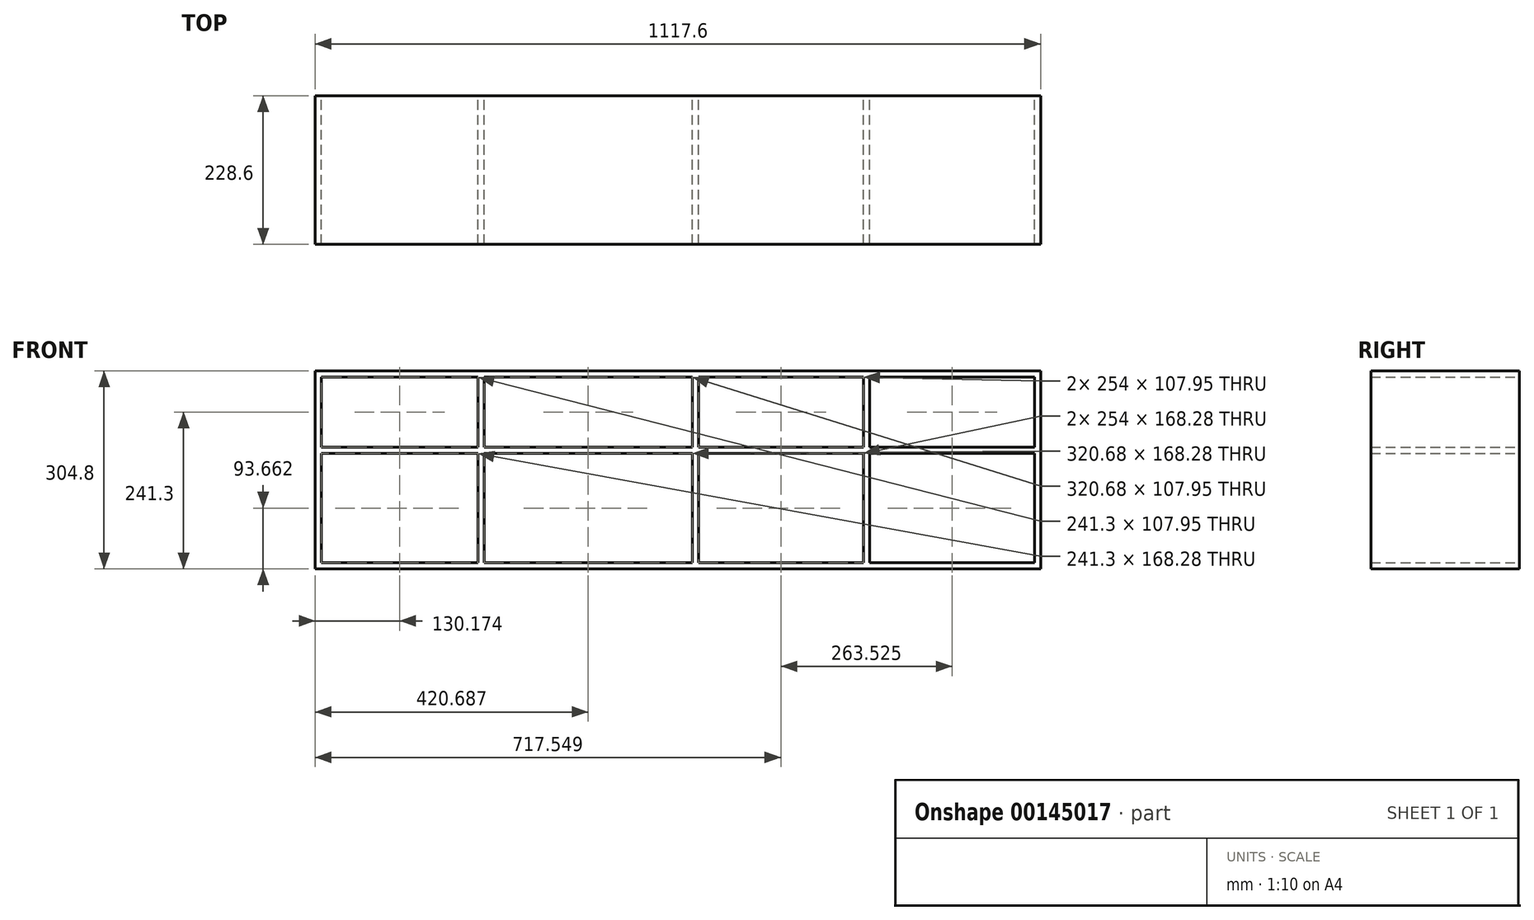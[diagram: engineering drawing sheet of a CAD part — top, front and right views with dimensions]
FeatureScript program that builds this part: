
annotation { "Feature Type Name" : "Feature", "Feature Type Description" : "" }
export const myFeature = defineFeature(function(context is Context, id is Id, definition is map)
    precondition{}
    {
        {
            var Q0;
            Q0=qCreatedBy(makeId("Front.planeOp"),FACE);
            var sketch = newSketch(context, id + "F0", { "sketchPlane" : qUnion([Q0])});
            skLineSegment(sketch, "E0.bottom", {"start": v(-515.76, 0) * mm, "end": v(601.84, 0) * mm});
            skLineSegment(sketch, "E0.top", {"start": v(-515.76, 304.8) * mm, "end": v(601.84, 304.8) * mm});
            skLineSegment(sketch, "E0.left", {"start": v(-515.76, 0) * mm, "end": v(-515.76, 304.8) * mm});
            skLineSegment(sketch, "E0.right", {"start": v(601.84, 0) * mm, "end": v(601.84, 304.8) * mm});
            skLineSegment(sketch, "E1.0", {"start": v(-506.24, 9.53) * mm, "end": v(-506.24, 295.28) * mm});
            skLineSegment(sketch, "E1.1", {"start": v(-506.24, 9.53) * mm, "end": v(592.31, 9.53) * mm});
            skLineSegment(sketch, "E1.2", {"start": v(592.31, 9.53) * mm, "end": v(592.31, 295.28) * mm});
            skLineSegment(sketch, "E1.3", {"start": v(-506.24, 295.28) * mm, "end": v(592.31, 295.28) * mm});
            skLineSegment(sketch, "E2.bottom", {"start": v(-264.94, 177.8) * mm, "end": v(-506.24, 177.8) * mm});
            skLineSegment(sketch, "E2.top", {"start": v(-264.94, 9.53) * mm, "end": v(-506.24, 9.53) * mm});
            skLineSegment(sketch, "E2.left", {"start": v(-264.94, 177.8) * mm, "end": v(-264.94, 9.53) * mm});
            skLineSegment(sketch, "E2.right", {"start": v(-506.24, 177.8) * mm, "end": v(-506.24, 9.53) * mm});
            skLineSegment(sketch, "E3.0", {"start": v(-255.41, 187.32) * mm, "end": v(-506.24, 187.32) * mm});
            skLineSegment(sketch, "E3.1", {"start": v(-255.41, 187.33) * mm, "end": v(-255.41, 9.53) * mm});
            skLineSegment(sketch, "E4", {"start": v(-255.41, 187.33) * mm, "end": v(-255.41, 295.28) * mm});
            skLineSegment(sketch, "E5.0", {"start": v(-264.94, 187.32) * mm, "end": v(-264.94, 295.28) * mm});
            skLineSegment(sketch, "E6", {"start": v(-255.41, 187.32) * mm, "end": v(592.31, 187.32) * mm});
            skLineSegment(sketch, "E7.0", {"start": v(-255.41, 177.8) * mm, "end": v(592.31, 177.8) * mm});
            skLineSegment(sketch, "E8", {"start": v(338.31, 177.8) * mm, "end": v(338.31, 9.53) * mm});
            skLineSegment(sketch, "E9.0", {"start": v(328.79, 177.8) * mm, "end": v(328.79, 9.53) * mm});
            skLineSegment(sketch, "E10", {"start": v(74.79, 177.8) * mm, "end": v(74.79, 9.53) * mm});
            skPoint(sketch, "E10.endSnap0", {"position": v(43.04, 9.53) * mm});
            skLineSegment(sketch, "E11.0", {"start": v(65.26, 177.8) * mm, "end": v(65.26, 9.53) * mm});
            skLineSegment(sketch, "E12", {"start": v(338.31, 177.8) * mm, "end": v(338.31, 295.28) * mm});
            skLineSegment(sketch, "E13", {"start": v(74.79, 177.8) * mm, "end": v(74.79, 295.28) * mm});
            skLineSegment(sketch, "E14.0", {"start": v(328.79, 177.8) * mm, "end": v(328.79, 295.28) * mm});
            skLineSegment(sketch, "E15.0", {"start": v(65.26, 177.8) * mm, "end": v(65.26, 295.28) * mm});
            skSolve(sketch);
        }
        {
            var Q0;
            Q0=makeQuery(id+"F0.imprint","IMPRINT",FACE,{"disambiguationData":[TD([[makeQuery(id+"F0.imprint","IMPRINT",EDGE,{"derivedFrom":sQuery(id+"F0.wireOp",EDGE,"E0.bottom")}),1.0]])]});
            var Q1;
            {var subQ1=sQuery(id+"F0.wireOp",EDGE,"E2.bottom");Q1=makeQuery(id+"F0.imprint","IMPRINT",FACE,{"disambiguationData":[TD([[makeQuery(id+"F0.imprint","IMPRINT",EDGE,{"derivedFrom":subQ1}),-1.0]])]});}
            var Q2;
            {var subQ0=sQuery(id+"F0.wireOp",EDGE,"E4");Q2=makeQuery(id+"F0.imprint","IMPRINT",FACE,{"disambiguationData":[TD([[makeQuery(id+"F0.imprint","IMPRINT",EDGE,{"derivedFrom":subQ0}),1.0]])]});}
            extrude(context, id + "F1", {"entities" : qUnion([Q0, Q1, Q2]), "depth" : 228.6 * mm});
        }
        {
            var Q0;
            {var subQ0=sQuery(id+"F0.wireOp",EDGE,"E6");Q0=makeQuery(id+"F0.imprint","IMPRINT",FACE,{"disambiguationData":[TD([[makeQuery(id+"F0.imprint","IMPRINT",EDGE,{"derivedFrom":subQ0}),-1.0]])]});}
            var Q1;
            Q1=makeQuery(id+"F1.opExtrude","CAP_FACE",FACE,{"disambiguationData":[OSD([sQuery(id+"F0.wireOp",EDGE,"E0.bottom"),sQuery(id+"F0.wireOp",EDGE,"E0.top"),sQuery(id+"F0.wireOp",EDGE,"E0.left"),sQuery(id+"F0.wireOp",EDGE,"E0.right"),sQuery(id+"F0.wireOp",EDGE,"E1.0"),sQuery(id+"F0.wireOp",EDGE,"E1.1"),sQuery(id+"F0.wireOp",EDGE,"E1.2"),sQuery(id+"F0.wireOp",EDGE,"E1.3"),sQuery(id+"F0.wireOp",EDGE,"E2.bottom"),sQuery(id+"F0.wireOp",EDGE,"E2.top"),sQuery(id+"F0.wireOp",EDGE,"E2.left"),sQuery(id+"F0.wireOp",EDGE,"E2.right"),sQuery(id+"F0.wireOp",EDGE,"E3.0"),sQuery(id+"F0.wireOp",EDGE,"E3.1"),sQuery(id+"F0.wireOp",EDGE,"E4"),sQuery(id+"F0.wireOp",EDGE,"E5.0")])],"isStart":false});
            extrude(context, id + "F2", {"entities" : qUnion([Q0]), "operationType" : NewBodyOperationType.ADD, "endBound" : BoundingType.UP_TO_SURFACE, "endBoundEntityFace" : qUnion([Q1]), "depth" : 25.4 * mm});
        }
        {
            var Q0;
            {var subQ0=sQuery(id+"F0.wireOp",EDGE,"E8");Q0=makeQuery(id+"F0.imprint","IMPRINT",FACE,{"disambiguationData":[TD([[makeQuery(id+"F0.imprint","IMPRINT",EDGE,{"derivedFrom":subQ0}),-1.0]])]});}
            var Q1;
            {var subQ0=sQuery(id+"F0.wireOp",EDGE,"E5.0");var subQ1=sQuery(id+"F0.wireOp",EDGE,"E4");var subQ2=sQuery(id+"F0.wireOp",EDGE,"E3.1");var subQ3=sQuery(id+"F0.wireOp",EDGE,"E3.0");var subQ4=sQuery(id+"F0.wireOp",EDGE,"E2.right");var subQ5=sQuery(id+"F0.wireOp",EDGE,"E2.left");var subQ6=sQuery(id+"F0.wireOp",EDGE,"E2.top");var subQ7=sQuery(id+"F0.wireOp",EDGE,"E2.bottom");var subQ8=sQuery(id+"F0.wireOp",EDGE,"E1.3");var subQ9=sQuery(id+"F0.wireOp",EDGE,"E1.2");var subQ10=sQuery(id+"F0.wireOp",EDGE,"E1.1");var subQ11=sQuery(id+"F0.wireOp",EDGE,"E1.0");var subQ12=sQuery(id+"F0.wireOp",EDGE,"E0.right");var subQ13=sQuery(id+"F0.wireOp",EDGE,"E0.left");var subQ14=sQuery(id+"F0.wireOp",EDGE,"E0.top");var subQ15=sQuery(id+"F0.wireOp",EDGE,"E0.bottom");Q1=makeQuery(id+"F2.boolean.opBoolean","MERGE",FACE,{"derivedFrom":[makeQuery(id+"F1.opExtrude","CAP_FACE",FACE,{"disambiguationData":[OSD([subQ15,subQ14,subQ13,subQ12,subQ11,subQ10,subQ9,subQ8,subQ7,subQ6,subQ5,subQ4,subQ3,subQ2,subQ1,subQ0])],"isStart":false}),makeQuery(id+"F2.opExtrude","CAP_FACE",FACE,{"disambiguationData":[OSD([subQ15,subQ14,subQ13,subQ12,subQ11,subQ10,subQ9,subQ8,subQ7,subQ6,subQ5,subQ4,subQ3,subQ2,subQ1,subQ0])],"isStart":false})]});}
            extrude(context, id + "F3", {"entities" : qUnion([Q0]), "operationType" : NewBodyOperationType.ADD, "endBound" : BoundingType.UP_TO_SURFACE, "endBoundEntityFace" : qUnion([Q1]), "depth" : 25.4 * mm});
        }
        {
            var Q0;
            {var subQ1=sQuery(id+"F0.wireOp",EDGE,"E7.0");var subQ4=sQuery(id+"F0.wireOp",EDGE,"E3.1");var subQ5=makeQuery(id+"F0.imprint","INTERSECT",VERTEX,{"derivedFrom":[subQ4,subQ1]});Q0=makeQuery(id+"F0.imprint","IMPRINT",FACE,{"disambiguationData":[TD([[makeQuery(id+"F0.imprint","IMPRINT",EDGE,{"disambiguationData":[TD([[subQ5,-1.0]])],"derivedFrom":subQ1}),1.0]])]});}
            var Q1;
            {var subQ0=sQuery(id+"F0.wireOp",EDGE,"E10");Q1=makeQuery(id+"F0.imprint","IMPRINT",FACE,{"disambiguationData":[TD([[makeQuery(id+"F0.imprint","IMPRINT",EDGE,{"derivedFrom":subQ0}),-1.0]])]});}
            var Q2;
            {var subQ0=sQuery(id+"F0.wireOp",EDGE,"E5.0");var subQ1=sQuery(id+"F0.wireOp",EDGE,"E4");var subQ2=sQuery(id+"F0.wireOp",EDGE,"E3.1");var subQ3=sQuery(id+"F0.wireOp",EDGE,"E3.0");var subQ4=sQuery(id+"F0.wireOp",EDGE,"E2.right");var subQ5=sQuery(id+"F0.wireOp",EDGE,"E2.left");var subQ6=sQuery(id+"F0.wireOp",EDGE,"E2.top");var subQ7=sQuery(id+"F0.wireOp",EDGE,"E2.bottom");var subQ8=sQuery(id+"F0.wireOp",EDGE,"E1.3");var subQ9=sQuery(id+"F0.wireOp",EDGE,"E1.2");var subQ10=sQuery(id+"F0.wireOp",EDGE,"E1.1");var subQ11=sQuery(id+"F0.wireOp",EDGE,"E1.0");var subQ12=sQuery(id+"F0.wireOp",EDGE,"E0.right");var subQ13=sQuery(id+"F0.wireOp",EDGE,"E0.left");var subQ14=sQuery(id+"F0.wireOp",EDGE,"E0.top");var subQ15=sQuery(id+"F0.wireOp",EDGE,"E0.bottom");Q2=makeQuery(id+"F3.boolean.opBoolean","MERGE",FACE,{"derivedFrom":[makeQuery(id+"F2.boolean.opBoolean","MERGE",FACE,{"derivedFrom":[makeQuery(id+"F1.opExtrude","CAP_FACE",FACE,{"disambiguationData":[OSD([subQ15,subQ14,subQ13,subQ12,subQ11,subQ10,subQ9,subQ8,subQ7,subQ6,subQ5,subQ4,subQ3,subQ2,subQ1,subQ0])],"isStart":false}),makeQuery(id+"F2.opExtrude","CAP_FACE",FACE,{"disambiguationData":[OSD([subQ15,subQ14,subQ13,subQ12,subQ11,subQ10,subQ9,subQ8,subQ7,subQ6,subQ5,subQ4,subQ3,subQ2,subQ1,subQ0])],"isStart":false})]}),makeQuery(id+"F3.opExtrude","CAP_FACE",FACE,{"disambiguationData":[OSD([subQ15,subQ14,subQ13,subQ12,subQ11,subQ10,subQ9,subQ8,subQ7,subQ6,subQ5,subQ4,subQ3,subQ2,subQ1,subQ0])],"isStart":false})]});}
            extrude(context, id + "F4", {"entities" : qUnion([Q0, Q1]), "operationType" : NewBodyOperationType.ADD, "endBound" : BoundingType.UP_TO_SURFACE, "endBoundEntityFace" : qUnion([Q2]), "depth" : 25.4 * mm});
        }
        {
            var Q0;
            {var subQ0=sQuery(id+"F0.wireOp",EDGE,"E13");var subQ1=sQuery(id+"F0.wireOp",EDGE,"E1.3");var subQ2=makeQuery(id+"F0.imprint","INTERSECT",VERTEX,{"derivedFrom":[subQ1,subQ0]});Q0=makeQuery(id+"F0.imprint","IMPRINT",FACE,{"disambiguationData":[TD([[makeQuery(id+"F0.imprint","IMPRINT",EDGE,{"disambiguationData":[TD([[subQ2,1.0]])],"derivedFrom":subQ1}),-1.0]])]});}
            var Q1;
            {var subQ0=sQuery(id+"F0.wireOp",EDGE,"E12");var subQ1=sQuery(id+"F0.wireOp",EDGE,"E1.3");var subQ2=makeQuery(id+"F0.imprint","INTERSECT",VERTEX,{"derivedFrom":[subQ1,subQ0]});Q1=makeQuery(id+"F0.imprint","IMPRINT",FACE,{"disambiguationData":[TD([[makeQuery(id+"F0.imprint","IMPRINT",EDGE,{"disambiguationData":[TD([[subQ2,1.0]])],"derivedFrom":subQ1}),-1.0]])]});}
            var Q2;
            {var subQ0=sQuery(id+"F0.wireOp",EDGE,"E1.1");var subQ1=sQuery(id+"F0.wireOp",EDGE,"E5.0");var subQ2=sQuery(id+"F0.wireOp",EDGE,"E4");var subQ3=sQuery(id+"F0.wireOp",EDGE,"E3.1");var subQ4=sQuery(id+"F0.wireOp",EDGE,"E3.0");var subQ5=sQuery(id+"F0.wireOp",EDGE,"E2.right");var subQ6=sQuery(id+"F0.wireOp",EDGE,"E2.left");var subQ7=sQuery(id+"F0.wireOp",EDGE,"E2.top");var subQ8=sQuery(id+"F0.wireOp",EDGE,"E2.bottom");var subQ9=sQuery(id+"F0.wireOp",EDGE,"E1.3");var subQ10=sQuery(id+"F0.wireOp",EDGE,"E1.2");var subQ11=sQuery(id+"F0.wireOp",EDGE,"E1.0");var subQ12=sQuery(id+"F0.wireOp",EDGE,"E0.right");var subQ13=sQuery(id+"F0.wireOp",EDGE,"E0.left");var subQ14=sQuery(id+"F0.wireOp",EDGE,"E0.top");var subQ15=sQuery(id+"F0.wireOp",EDGE,"E0.bottom");Q2=makeQuery(id+"F4.boolean.opBoolean","MERGE",FACE,{"derivedFrom":[makeQuery(id+"F3.boolean.opBoolean","MERGE",FACE,{"derivedFrom":[makeQuery(id+"F2.boolean.opBoolean","MERGE",FACE,{"derivedFrom":[makeQuery(id+"F1.opExtrude","CAP_FACE",FACE,{"disambiguationData":[OSD([subQ15,subQ14,subQ13,subQ12,subQ11,subQ0,subQ10,subQ9,subQ8,subQ7,subQ6,subQ5,subQ4,subQ3,subQ2,subQ1])],"isStart":false}),makeQuery(id+"F2.opExtrude","CAP_FACE",FACE,{"disambiguationData":[OSD([subQ15,subQ14,subQ13,subQ12,subQ11,subQ0,subQ10,subQ9,subQ8,subQ7,subQ6,subQ5,subQ4,subQ3,subQ2,subQ1])],"isStart":false})]}),makeQuery(id+"F3.opExtrude","CAP_FACE",FACE,{"disambiguationData":[OSD([subQ15,subQ14,subQ13,subQ12,subQ11,subQ0,subQ10,subQ9,subQ8,subQ7,subQ6,subQ5,subQ4,subQ3,subQ2,subQ1])],"isStart":false})]}),makeQuery(id+"F4.opExtrude","CAP_FACE",FACE,{"disambiguationData":[OSD([subQ15,subQ14,subQ13,subQ12,subQ11,subQ0,subQ10,subQ9,subQ8,subQ7,subQ6,subQ5,subQ4,subQ3,subQ2,subQ1]),ownerDisambiguation([makeQuery(id+"F4.opExtrude","SWEPT_BODY",BODY,{"disambiguationData":[OSD([subQ0,sQuery(id+"F0.wireOp",EDGE,"E7.0"),sQuery(id+"F0.wireOp",EDGE,"E10"),sQuery(id+"F0.wireOp",EDGE,"E11.0")])]})])],"isStart":false})]});}
            extrude(context, id + "F5", {"entities" : qUnion([Q0, Q1]), "operationType" : NewBodyOperationType.ADD, "endBound" : BoundingType.UP_TO_SURFACE, "endBoundEntityFace" : qUnion([Q2]), "depth" : 25.4 * mm});
        }
    });
